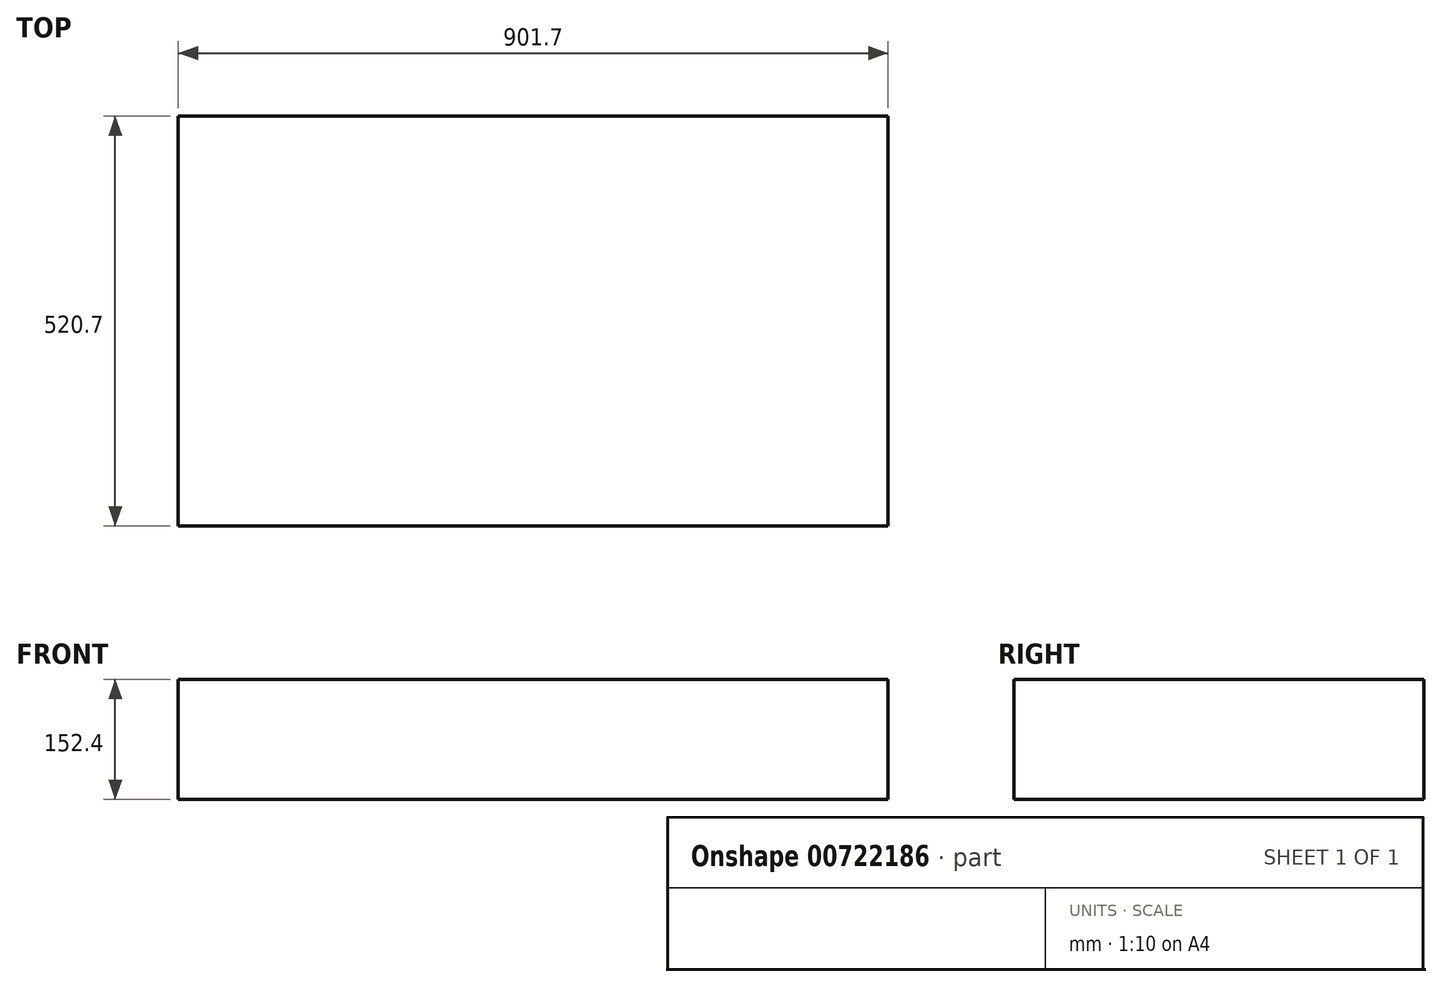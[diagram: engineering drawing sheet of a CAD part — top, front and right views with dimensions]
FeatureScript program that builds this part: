
annotation { "Feature Type Name" : "Feature", "Feature Type Description" : "" }
export const myFeature = defineFeature(function(context is Context, id is Id, definition is map)
    precondition{}
    {
        {
            var Q0;
            Q0=qCreatedBy(makeId("Top.planeOp"),FACE);
            var sketch = newSketch(context, id + "F0", { "sketchPlane" : qUnion([Q0])});
            skLineSegment(sketch, "E0.bottom", {"start": v(-450.85, 0) * mm, "end": v(450.85, 0) * mm});
            skLineSegment(sketch, "E0.top", {"start": v(-450.85, 520.7) * mm, "end": v(450.85, 520.7) * mm});
            skLineSegment(sketch, "E0.left", {"start": v(-450.85, 0) * mm, "end": v(-450.85, 520.7) * mm});
            skLineSegment(sketch, "E0.right", {"start": v(450.85, 0) * mm, "end": v(450.85, 520.7) * mm});
            skLineSegment(sketch, "E1", {"start": v(0, 432.9) * mm, "end": v(0, 0) * mm, "construction": true});
            skSolve(sketch);
        }
        {
            var Q0;
            Q0 = qSketchRegion(id + "F0", true);
            extrude(context, id + "F1", {"entities" : qUnion([Q0]), "depth" : 152.4 * mm, "offsetDistance" : 25.4 * mm});
        }
    });
